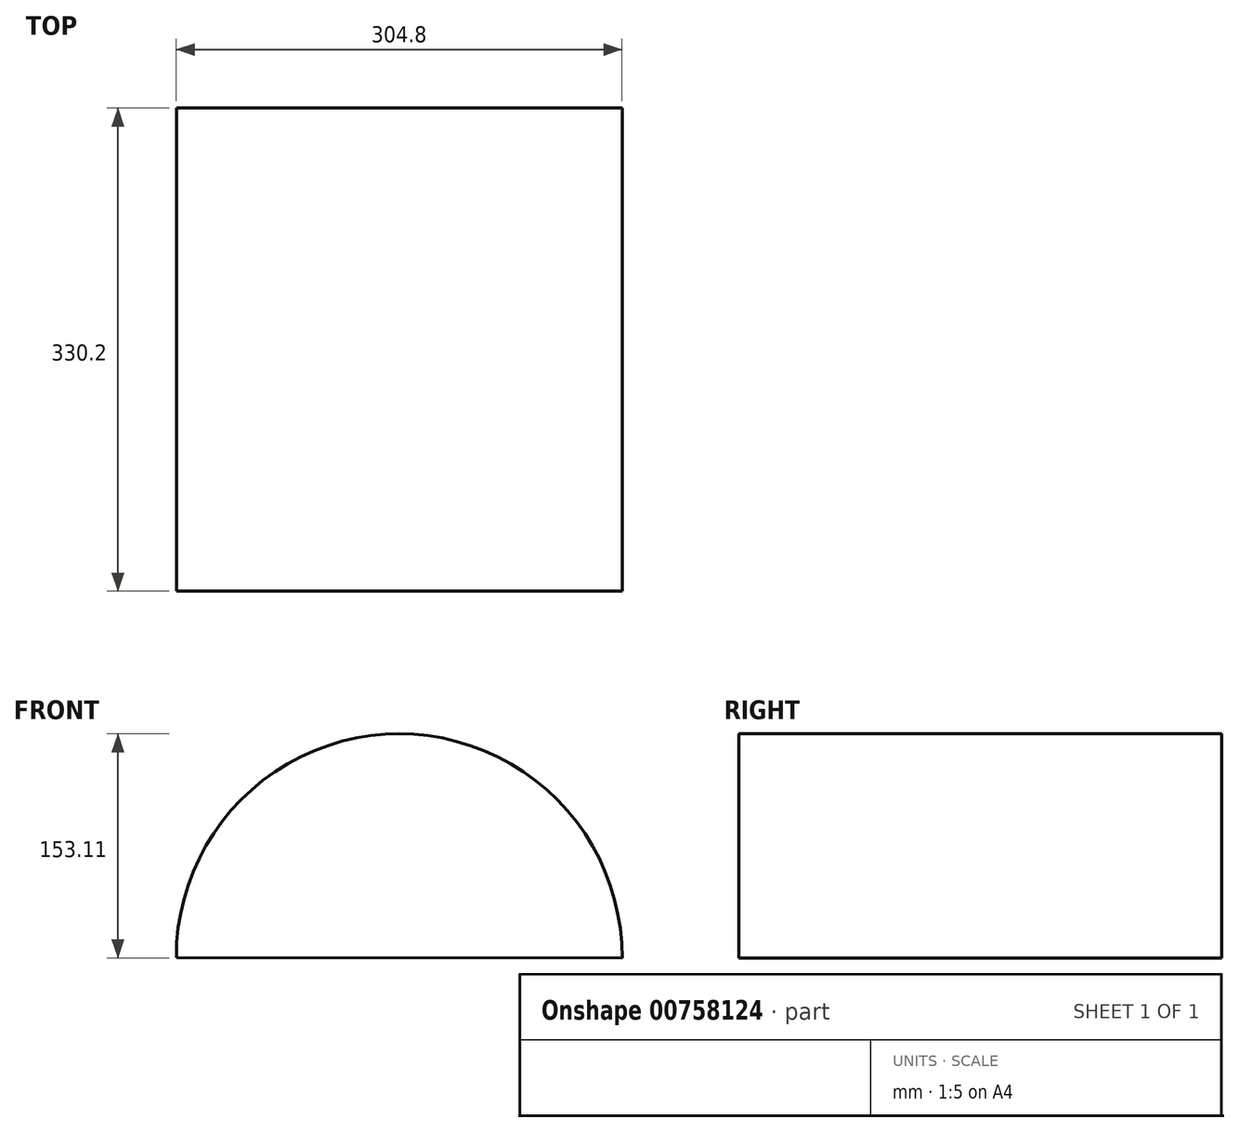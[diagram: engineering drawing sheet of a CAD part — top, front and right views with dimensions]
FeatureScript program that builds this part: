
annotation { "Feature Type Name" : "Feature", "Feature Type Description" : "" }
export const myFeature = defineFeature(function(context is Context, id is Id, definition is map)
    precondition{}
    {
        {
            var Q0;
            Q0=qCreatedBy(makeId("Front.planeOp"),FACE);
            var sketch = newSketch(context, id + "F0", { "sketchPlane" : qUnion([Q0])});
            skLineSegment(sketch, "E0", {"start": v(-123.55, 7.36) * mm, "end": v(181.25, 7.36) * mm});
            skArc(sketch, "E1", {"start": v(181.25, 7.36) * mm, "mid": v(28.92, 160.47) * mm, "end": v(-123.54, 7.5) * mm});
            skLineSegment(sketch, "E2", {"start": v(-123.54, 7.5) * mm, "end": v(181.25, 7.36) * mm});
            skSolve(sketch);
        }
        {
            var Q0;
            Q0 = qSketchRegion(id + "F0", true);
            extrude(context, id + "F1", {"entities" : qUnion([Q0]), "depth" : 330.2 * mm, "offsetDistance" : 25.4 * mm});
        }
    });
